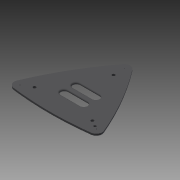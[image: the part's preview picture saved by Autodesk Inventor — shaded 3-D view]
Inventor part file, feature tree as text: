
AUTODESK INVENTOR PART (.ipt)
format: ipt  version: 2013 (Build 170138000, 138)  size: 200,192 bytes
history: native  units: mm
features: extrude x5, sketch x5, pattern_circular x1, fillet x1
ambient origin geometry x8: Origin, YZ Plane, XZ Plane, XY Plane, X Axis, Y Axis, Z Axis, Center Point
feature tree (12):
  extrude  "Extrusion2"  Depth=250.0mm
  extrude  "Extrusion9"  Depth=8.5mm
  extrude  "Extrusion10"  Depth=60.325mm
  pattern_circular  "Circular Pattern1"  [2 undecoded]
  extrude  "Extrusion11"  Depth=23.0mm
  extrude  "Extrusion12"  Depth=7.9375mm TaperAngle=0.0deg
  fillet  "Fillet2"  Radius=15.0mm
  sketch  "Sketch1"  dims[d0=300.0mm d1=250.0mm]
  sketch  "Sketch8"  dims[d2=3.175mm d3=8.5mm]
  sketch  "Sketch9"  dims[d4=50.0mm d5=60.325mm]
  sketch  "Sketch10"  dims[d6=25.0mm]
  sketch  "Sketch11"  dims[d9=3.175mm d10=12.5mm d11=0.0mm d34=23.0mm d37=7.9375mm d38=0.0mm d39=15.0mm d41=0.28125mm d42=0.0mm d43=30.0mm d44=360.0deg d46=25.0mm d48=100.0mm d49=18.75mm d50=10.0mm d51=0.0mm d52=25.0mm d54=50.0mm d55=10.0mm d56=0.0mm d57=6.35mm]
note: 2 required parameter values undecoded (feature->parameter linkage not recoverable at this tier; creation-order binding heuristic only, values carry confidence <= 0.55)
